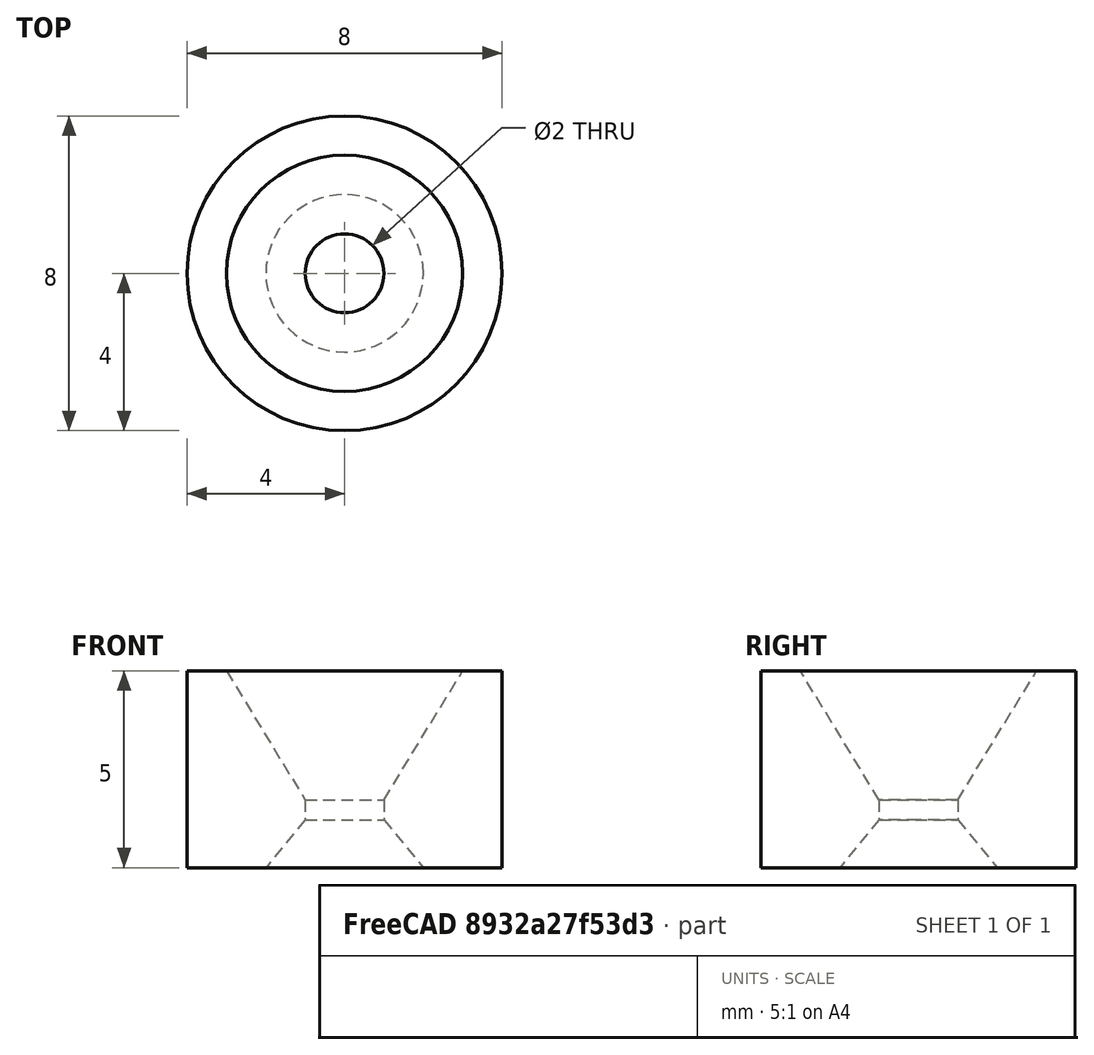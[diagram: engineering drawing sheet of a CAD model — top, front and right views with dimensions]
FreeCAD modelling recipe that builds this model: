
FCSTD DOCUMENT  (FreeCAD 0.18R16146 (Git))
Label: nozzle_small
Comment: # 2020-08-04 16:27:03: read from <userpath>/repositories/sussex_neuro/Olfactometer/hardware/mechanics/from_raiser_et_al/nozzle_big.ipt
License: All rights reserved
LicenseURL: http://en.wikipedia.org/wiki/All_rights_reserved
objects: Sketcher::SketchObject×2, Spreadsheet::Sheet×1, Part::Revolution×1
note: 3 computed .brp shape members not serialized (recipe doc carries the construction recipe); baked Part::Feature solids carry a one-line shape summary decoded from their .brp

FEATURE [Spreadsheet::Sheet] Parameters
  cells = A1=Parameter; B1=Value; C1=Fromula; D1=Tolerance; E1=Comment; A2=d13; B2(d13_)=90; C2=90°; D2=NOMINAL; A3=d16; B3(d16_)=1; C3=1mm; D3=NOMINAL; A4=d17; B4(d17_)=0.2; C4=0.2mm; D4=NOMINAL; A5=d18; B5(d18_)=2; C5=2mm; D5=NOMINAL; A6=d20; B6(d20_)=0.5; C6=0.5mm; D6=NOMINAL; A7=d21; B7(d21_)=2; C7=2mm; D7=NOMINAL; A8=d22; B8(d22_)=0; C8=0mm; D8=NOMINAL; A9=d23; B9(d23_)=20; C9=20mm; D9=NOMINAL; A10=d24; B10(d24_)=1; C10=1mm; D10=NOMINAL; A11=d25; B11(d25_)=4; C11=4mm; D11=NOMINAL; A12=d26; B12(d26_)=0.5; C12=0.5mm; D12=NOMINAL; A13=d27; B13(d27_)=2; C13=2mm; D13=NOMINAL; A14=d28; B14(d28_)=0; C14=0mm; D14=NOMINAL; A15=d29; B15(d29_)=20; C15=20mm; D15=NOMINAL; A16=d30; B16(d30_)=0.5; C16=0.5mm; D16=NOMINAL; A17=d31; B17(d31_)=2; C17=2mm; D17=NOMINAL; A18=d32; B18(d32_)=0; C18=0mm; D18=NOMINAL; A19=d33; B19(d33_)=20; C19=20mm; D19=NOMINAL; A20=d4; B20(d4_)=5; C20=5mm; D20=NOMINAL
FEATURE [Sketcher::SketchObject] Sketch2
  Placement = pos=(0,0,0) rot=(0,0.707107,0.707107;3.14159rad)
  sketch-geometry (8):
    g0: LineSegment StartX=4 StartY=0 StartZ=0 EndX=4 EndY=5 EndZ=0
    g1: LineSegment StartX=7e-16 StartY=-0.993601 StartZ=0 EndX=-1.5e-15 EndY=4.43052 EndZ=0
    g2: LineSegment StartX=4 StartY=5 StartZ=0 EndX=4 EndY=0 EndZ=0
    g3: LineSegment StartX=1 StartY=1.21846 StartZ=0 EndX=1 EndY=1.71846 EndZ=0
    g4: LineSegment StartX=1 StartY=1.21846 StartZ=0 EndX=2 EndY=-2.2e-15 EndZ=0
    g5: LineSegment StartX=2 StartY=-2.3e-15 StartZ=0 EndX=4 EndY=0 EndZ=0
    g6: LineSegment StartX=4 StartY=5 StartZ=0 EndX=3 EndY=5 EndZ=0
    g7: LineSegment StartX=3 StartY=5 StartZ=0 EndX=1 EndY=1.71846 EndZ=0
  constraints (7):
    c: Parallel(g2,g3)
    c: Perpendicular(g3,g5)
    c: Parallel(g5,g6)
    c: Coincident(g0,g2)
    c: Coincident(g0,g5)
    c: Coincident(g0,g2)
    c: Coincident(g0,g6)
FEATURE [Sketcher::SketchObject] Sketch2_bp
  Placement = pos=(0,0,0) rot=(0,0.707107,0.707107;3.14159rad)
  sketch-geometry (6):
    g0: LineSegment StartX=4 StartY=0 StartZ=0 EndX=4 EndY=5 EndZ=0
    g1: LineSegment StartX=4 StartY=5 StartZ=0 EndX=3 EndY=5 EndZ=0
    g2: LineSegment StartX=3 StartY=5 StartZ=0 EndX=1 EndY=1.71846 EndZ=0
    g3: LineSegment StartX=1 StartY=1.71846 StartZ=0 EndX=1 EndY=1.21846 EndZ=0
    g4: LineSegment StartX=1 StartY=1.21846 StartZ=0 EndX=2 EndY=-2.2e-15 EndZ=0
    g5: LineSegment StartX=2 StartY=-2.3e-15 StartZ=0 EndX=4 EndY=0 EndZ=0
FEATURE [Part::Revolution] Revolution2
  Angle = 360
  Axis = (2e-16,0,0.542412)
  Base = (-7e-16,0,-0.993601)
  FaceMakerClass = Part::FaceMakerBullseye
  Solid = true
  Source = -> Sketch2_bp
  Symmetric = false
